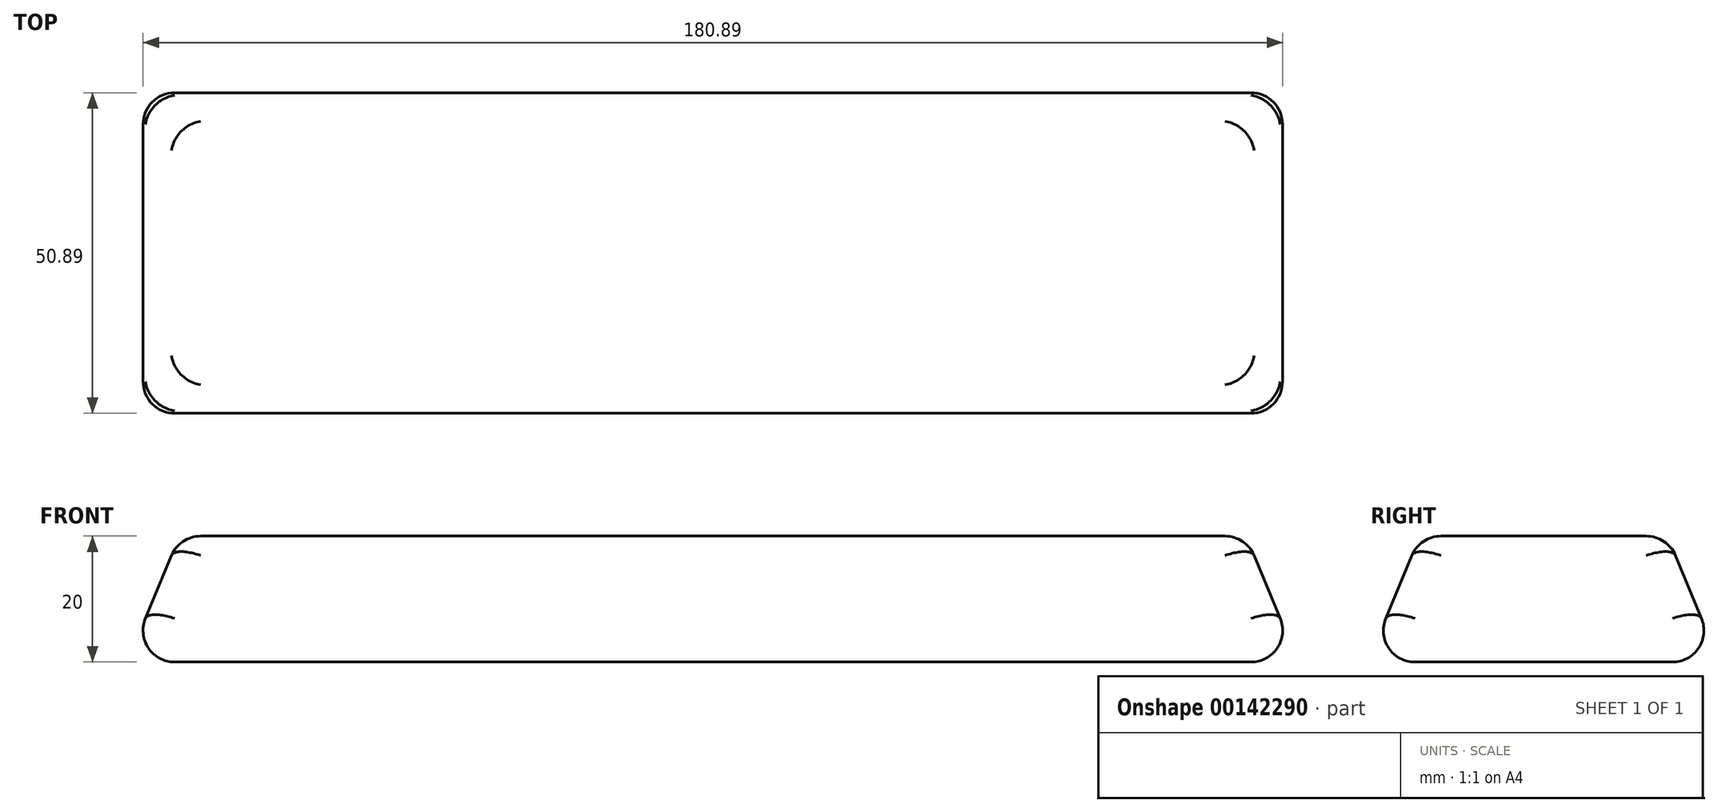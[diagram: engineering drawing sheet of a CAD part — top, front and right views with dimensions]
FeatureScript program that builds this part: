
annotation { "Feature Type Name" : "Feature", "Feature Type Description" : "" }
export const myFeature = defineFeature(function(context is Context, id is Id, definition is map)
    precondition{}
    {
        {
            var Q0;
            Q0=qCreatedBy(makeId("Top.planeOp"),FACE);
            var sketch = newSketch(context, id + "F0", { "sketchPlane" : qUnion([Q0])});
            skLineSegment(sketch, "E0.bottom", {"start": v(120, 55) * mm, "end": v(-120, 55) * mm});
            skLineSegment(sketch, "E0.top", {"start": v(120, -55) * mm, "end": v(-120, -55) * mm});
            skLineSegment(sketch, "E0.left", {"start": v(120, 55) * mm, "end": v(120, -55) * mm});
            skLineSegment(sketch, "E0.right", {"start": v(-120, 55) * mm, "end": v(-120, -55) * mm});
            skPoint(sketch, "E0.middle", {"position": v(0, 0) * mm});
            skSolve(sketch);
        }
        {
            var Q0;
            Q0=makeQuery(id+"F0.imprint","IMPRINT",FACE,{"disambiguationData":[TD([[makeQuery(id+"F0.imprint","IMPRINT",EDGE,{"derivedFrom":sQuery(id+"F0.wireOp",EDGE,"E0.bottom")}),1.0]])]});
            extrude(context, id + "F1", {"entities" : qUnion([Q0]), "depth" : 20 * mm});
        }
        {
            var Q0;
            Q0=makeQuery(id+"F1.opExtrude","CAP_EDGE",EDGE,{"disambiguationData":[OSD([sQuery(id+"F0.wireOp",EDGE,"E0.top")])],"isStart":false});
            chamfer(context, id + "F2", {"entities" : qUnion([Q0]), "chamferType" : ChamferType.OFFSET_ANGLE, "width" : 50 * mm, "oppositeDirection" : false, "angle" : 22.5 * degree, "tangentPropagation" : true});
        }
        {
            var Q0;
            Q0=makeQuery(id+"F1.opExtrude","CAP_EDGE",EDGE,{"disambiguationData":[OSD([sQuery(id+"F0.wireOp",EDGE,"E0.bottom")])],"isStart":false});
            chamfer(context, id + "F3", {"entities" : qUnion([Q0]), "chamferType" : ChamferType.OFFSET_ANGLE, "width" : 50 * mm, "oppositeDirection" : false, "angle" : 67.5 * degree, "tangentPropagation" : true});
        }
        {
            var Q0;
            Q0=makeQuery(id+"F1.opExtrude","CAP_EDGE",EDGE,{"disambiguationData":[OSD([sQuery(id+"F0.wireOp",EDGE,"E0.left")])],"isStart":false});
            chamfer(context, id + "F4", {"entities" : qUnion([Q0]), "chamferType" : ChamferType.OFFSET_ANGLE, "width" : 50 * mm, "oppositeDirection" : false, "angle" : 22.5 * degree, "tangentPropagation" : true});
        }
        {
            var Q0;
            Q0=makeQuery(id+"F1.opExtrude","CAP_EDGE",EDGE,{"disambiguationData":[OSD([sQuery(id+"F0.wireOp",EDGE,"E0.right")])],"isStart":false});
            chamfer(context, id + "F5", {"entities" : qUnion([Q0]), "chamferType" : ChamferType.OFFSET_ANGLE, "width" : 50 * mm, "oppositeDirection" : false, "angle" : 67.5 * degree, "tangentPropagation" : true});
        }
        {
            var Q0;
            Q0=makeQuery(id+"F4.opChamfer","BLEND_EDGE",EDGE,{"blendedFrom":[makeQuery(id+"F1.opExtrude","CAP_EDGE",EDGE,{"disambiguationData":[OSD([sQuery(id+"F0.wireOp",EDGE,"E0.left")])],"isStart":false}),makeQuery(id+"F2.opChamfer","BLEND_FACE",FACE,{"disambiguationData":[OSD([sQuery(id+"F0.wireOp",EDGE,"E0.top")])]})],"blendedInto":[makeQuery(id+"F2.opChamfer","BLEND_FACE",FACE,{"disambiguationData":[OSD([sQuery(id+"F0.wireOp",EDGE,"E0.top")])]})]});
            var Q1;
            {var subQ0=sQuery(id+"F0.wireOp",EDGE,"E0.left");Q1=makeQuery(id+"F4.opChamfer","BLEND_EDGE",EDGE,{"blendedFrom":[makeQuery(id+"F1.opExtrude","CAP_EDGE",EDGE,{"disambiguationData":[OSD([subQ0])],"isStart":false}),makeQuery(id+"F1.opExtrude","CAP_FACE",FACE,{"disambiguationData":[OSD([sQuery(id+"F0.wireOp",EDGE,"E0.bottom"),sQuery(id+"F0.wireOp",EDGE,"E0.top"),subQ0,sQuery(id+"F0.wireOp",EDGE,"E0.right")])],"isStart":false})],"blendedInto":[makeQuery(id+"F1.opExtrude","CAP_FACE",FACE,{"disambiguationData":[OSD([sQuery(id+"F0.wireOp",EDGE,"E0.bottom"),sQuery(id+"F0.wireOp",EDGE,"E0.top"),subQ0,sQuery(id+"F0.wireOp",EDGE,"E0.right")])],"isStart":false})]});}
            var Q2;
            {var subQ0=sQuery(id+"F0.wireOp",EDGE,"E0.top");Q2=makeQuery(id+"F2.opChamfer","BLEND_EDGE",EDGE,{"blendedFrom":[makeQuery(id+"F1.opExtrude","CAP_EDGE",EDGE,{"disambiguationData":[OSD([subQ0])],"isStart":false}),makeQuery(id+"F1.opExtrude","CAP_FACE",FACE,{"disambiguationData":[OSD([sQuery(id+"F0.wireOp",EDGE,"E0.bottom"),subQ0,sQuery(id+"F0.wireOp",EDGE,"E0.left"),sQuery(id+"F0.wireOp",EDGE,"E0.right")])],"isStart":false})],"blendedInto":[makeQuery(id+"F1.opExtrude","CAP_FACE",FACE,{"disambiguationData":[OSD([sQuery(id+"F0.wireOp",EDGE,"E0.bottom"),subQ0,sQuery(id+"F0.wireOp",EDGE,"E0.left"),sQuery(id+"F0.wireOp",EDGE,"E0.right")])],"isStart":false})]});}
            var Q3;
            Q3=makeQuery(id+"F5.opChamfer","BLEND_EDGE",EDGE,{"blendedFrom":[makeQuery(id+"F1.opExtrude","CAP_EDGE",EDGE,{"disambiguationData":[OSD([sQuery(id+"F0.wireOp",EDGE,"E0.right")])],"isStart":false}),makeQuery(id+"F2.opChamfer","BLEND_FACE",FACE,{"disambiguationData":[OSD([sQuery(id+"F0.wireOp",EDGE,"E0.top")])]})],"blendedInto":[makeQuery(id+"F2.opChamfer","BLEND_FACE",FACE,{"disambiguationData":[OSD([sQuery(id+"F0.wireOp",EDGE,"E0.top")])]})]});
            var Q4;
            {var subQ0=sQuery(id+"F0.wireOp",EDGE,"E0.right");Q4=makeQuery(id+"F5.opChamfer","BLEND_EDGE",EDGE,{"blendedFrom":[makeQuery(id+"F1.opExtrude","CAP_EDGE",EDGE,{"disambiguationData":[OSD([subQ0])],"isStart":false}),makeQuery(id+"F1.opExtrude","CAP_FACE",FACE,{"disambiguationData":[OSD([sQuery(id+"F0.wireOp",EDGE,"E0.bottom"),sQuery(id+"F0.wireOp",EDGE,"E0.top"),sQuery(id+"F0.wireOp",EDGE,"E0.left"),subQ0])],"isStart":false})],"blendedInto":[makeQuery(id+"F1.opExtrude","CAP_FACE",FACE,{"disambiguationData":[OSD([sQuery(id+"F0.wireOp",EDGE,"E0.bottom"),sQuery(id+"F0.wireOp",EDGE,"E0.top"),sQuery(id+"F0.wireOp",EDGE,"E0.left"),subQ0])],"isStart":false})]});}
            var Q5;
            Q5=makeQuery(id+"F5.opChamfer","BLEND_EDGE",EDGE,{"blendedFrom":[makeQuery(id+"F1.opExtrude","CAP_EDGE",EDGE,{"disambiguationData":[OSD([sQuery(id+"F0.wireOp",EDGE,"E0.right")])],"isStart":false}),makeQuery(id+"F3.opChamfer","BLEND_FACE",FACE,{"disambiguationData":[OSD([sQuery(id+"F0.wireOp",EDGE,"E0.bottom")])]})],"blendedInto":[makeQuery(id+"F3.opChamfer","BLEND_FACE",FACE,{"disambiguationData":[OSD([sQuery(id+"F0.wireOp",EDGE,"E0.bottom")])]})]});
            var Q6;
            Q6=makeQuery(id+"F4.opChamfer","BLEND_EDGE",EDGE,{"blendedFrom":[makeQuery(id+"F1.opExtrude","CAP_EDGE",EDGE,{"disambiguationData":[OSD([sQuery(id+"F0.wireOp",EDGE,"E0.left")])],"isStart":false}),makeQuery(id+"F3.opChamfer","BLEND_FACE",FACE,{"disambiguationData":[OSD([sQuery(id+"F0.wireOp",EDGE,"E0.bottom")])]})],"blendedInto":[makeQuery(id+"F3.opChamfer","BLEND_FACE",FACE,{"disambiguationData":[OSD([sQuery(id+"F0.wireOp",EDGE,"E0.bottom")])]})]});
            var Q7;
            {var subQ0=sQuery(id+"F0.wireOp",EDGE,"E0.bottom");Q7=makeQuery(id+"F3.opChamfer","BLEND_EDGE",EDGE,{"blendedFrom":[makeQuery(id+"F1.opExtrude","CAP_EDGE",EDGE,{"disambiguationData":[OSD([subQ0])],"isStart":false}),makeQuery(id+"F1.opExtrude","CAP_FACE",FACE,{"disambiguationData":[OSD([subQ0,sQuery(id+"F0.wireOp",EDGE,"E0.top"),sQuery(id+"F0.wireOp",EDGE,"E0.left"),sQuery(id+"F0.wireOp",EDGE,"E0.right")])],"isStart":false})],"blendedInto":[makeQuery(id+"F1.opExtrude","CAP_FACE",FACE,{"disambiguationData":[OSD([subQ0,sQuery(id+"F0.wireOp",EDGE,"E0.top"),sQuery(id+"F0.wireOp",EDGE,"E0.left"),sQuery(id+"F0.wireOp",EDGE,"E0.right")])],"isStart":false})]});}
            fillet(context, id + "F6", {"entities" : qUnion([Q0, Q1, Q2, Q3, Q4, Q5, Q6, Q7]), "radius" : 5 * mm, "tangentPropagation" : true, "allowEdgeOverflow" : false});
        }
        {
            var Q0;
            {var subQ0=sQuery(id+"F0.wireOp",EDGE,"E0.bottom");Q0=makeQuery(id+"F3.opChamfer","BLEND_EDGE",EDGE,{"blendedFrom":[makeQuery(id+"F1.opExtrude","CAP_EDGE",EDGE,{"disambiguationData":[OSD([subQ0])],"isStart":false}),makeQuery(id+"F1.opExtrude","CAP_FACE",FACE,{"disambiguationData":[OSD([subQ0,sQuery(id+"F0.wireOp",EDGE,"E0.top"),sQuery(id+"F0.wireOp",EDGE,"E0.left"),sQuery(id+"F0.wireOp",EDGE,"E0.right")])],"isStart":true})],"blendedInto":[makeQuery(id+"F1.opExtrude","CAP_FACE",FACE,{"disambiguationData":[OSD([subQ0,sQuery(id+"F0.wireOp",EDGE,"E0.top"),sQuery(id+"F0.wireOp",EDGE,"E0.left"),sQuery(id+"F0.wireOp",EDGE,"E0.right")])],"isStart":true})]});}
            var Q1;
            {var subQ0=sQuery(id+"F0.wireOp",EDGE,"E0.right");Q1=makeQuery(id+"F5.opChamfer","BLEND_EDGE",EDGE,{"blendedFrom":[makeQuery(id+"F1.opExtrude","CAP_EDGE",EDGE,{"disambiguationData":[OSD([subQ0])],"isStart":false}),makeQuery(id+"F1.opExtrude","CAP_FACE",FACE,{"disambiguationData":[OSD([sQuery(id+"F0.wireOp",EDGE,"E0.bottom"),sQuery(id+"F0.wireOp",EDGE,"E0.top"),sQuery(id+"F0.wireOp",EDGE,"E0.left"),subQ0])],"isStart":true})],"blendedInto":[makeQuery(id+"F1.opExtrude","CAP_FACE",FACE,{"disambiguationData":[OSD([sQuery(id+"F0.wireOp",EDGE,"E0.bottom"),sQuery(id+"F0.wireOp",EDGE,"E0.top"),sQuery(id+"F0.wireOp",EDGE,"E0.left"),subQ0])],"isStart":true})]});}
            var Q2;
            {var subQ0=sQuery(id+"F0.wireOp",EDGE,"E0.top");Q2=makeQuery(id+"F2.opChamfer","BLEND_EDGE",EDGE,{"blendedFrom":[makeQuery(id+"F1.opExtrude","CAP_EDGE",EDGE,{"disambiguationData":[OSD([subQ0])],"isStart":false}),makeQuery(id+"F1.opExtrude","CAP_FACE",FACE,{"disambiguationData":[OSD([sQuery(id+"F0.wireOp",EDGE,"E0.bottom"),subQ0,sQuery(id+"F0.wireOp",EDGE,"E0.left"),sQuery(id+"F0.wireOp",EDGE,"E0.right")])],"isStart":true})],"blendedInto":[makeQuery(id+"F1.opExtrude","CAP_FACE",FACE,{"disambiguationData":[OSD([sQuery(id+"F0.wireOp",EDGE,"E0.bottom"),subQ0,sQuery(id+"F0.wireOp",EDGE,"E0.left"),sQuery(id+"F0.wireOp",EDGE,"E0.right")])],"isStart":true})]});}
            var Q3;
            {var subQ0=sQuery(id+"F0.wireOp",EDGE,"E0.left");Q3=makeQuery(id+"F4.opChamfer","BLEND_EDGE",EDGE,{"blendedFrom":[makeQuery(id+"F1.opExtrude","CAP_EDGE",EDGE,{"disambiguationData":[OSD([subQ0])],"isStart":false}),makeQuery(id+"F1.opExtrude","CAP_FACE",FACE,{"disambiguationData":[OSD([sQuery(id+"F0.wireOp",EDGE,"E0.bottom"),sQuery(id+"F0.wireOp",EDGE,"E0.top"),subQ0,sQuery(id+"F0.wireOp",EDGE,"E0.right")])],"isStart":true})],"blendedInto":[makeQuery(id+"F1.opExtrude","CAP_FACE",FACE,{"disambiguationData":[OSD([sQuery(id+"F0.wireOp",EDGE,"E0.bottom"),sQuery(id+"F0.wireOp",EDGE,"E0.top"),subQ0,sQuery(id+"F0.wireOp",EDGE,"E0.right")])],"isStart":true})]});}
            fillet(context, id + "F7", {"entities" : qUnion([Q0, Q1, Q2, Q3]), "radius" : 5 * mm, "tangentPropagation" : true, "allowEdgeOverflow" : false});
        }
    });
